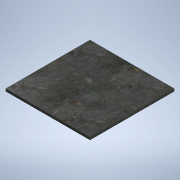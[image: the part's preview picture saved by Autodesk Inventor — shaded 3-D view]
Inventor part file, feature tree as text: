
AUTODESK INVENTOR PART (.ipt)
format: ipt  version: 2020.5 (Build 245400000, 400)  size: 110,080 bytes
history: native  units: mm
features: other x1, extrude x1, sketch x1
ambient origin geometry x8: Origin, YZ Plane, XZ Plane, XY Plane, X Axis, Y Axis, Z Axis, Center Point
bodies: Body1 (feature_tree)
feature tree (3):
  other  "Sólido1"
  extrude  "Extrusión1"  Depth=254.0mm
  sketch  "Boceto1"  dims[d0=254.0mm d1=254.0mm d2=7.62mm d3=0.0mm]
